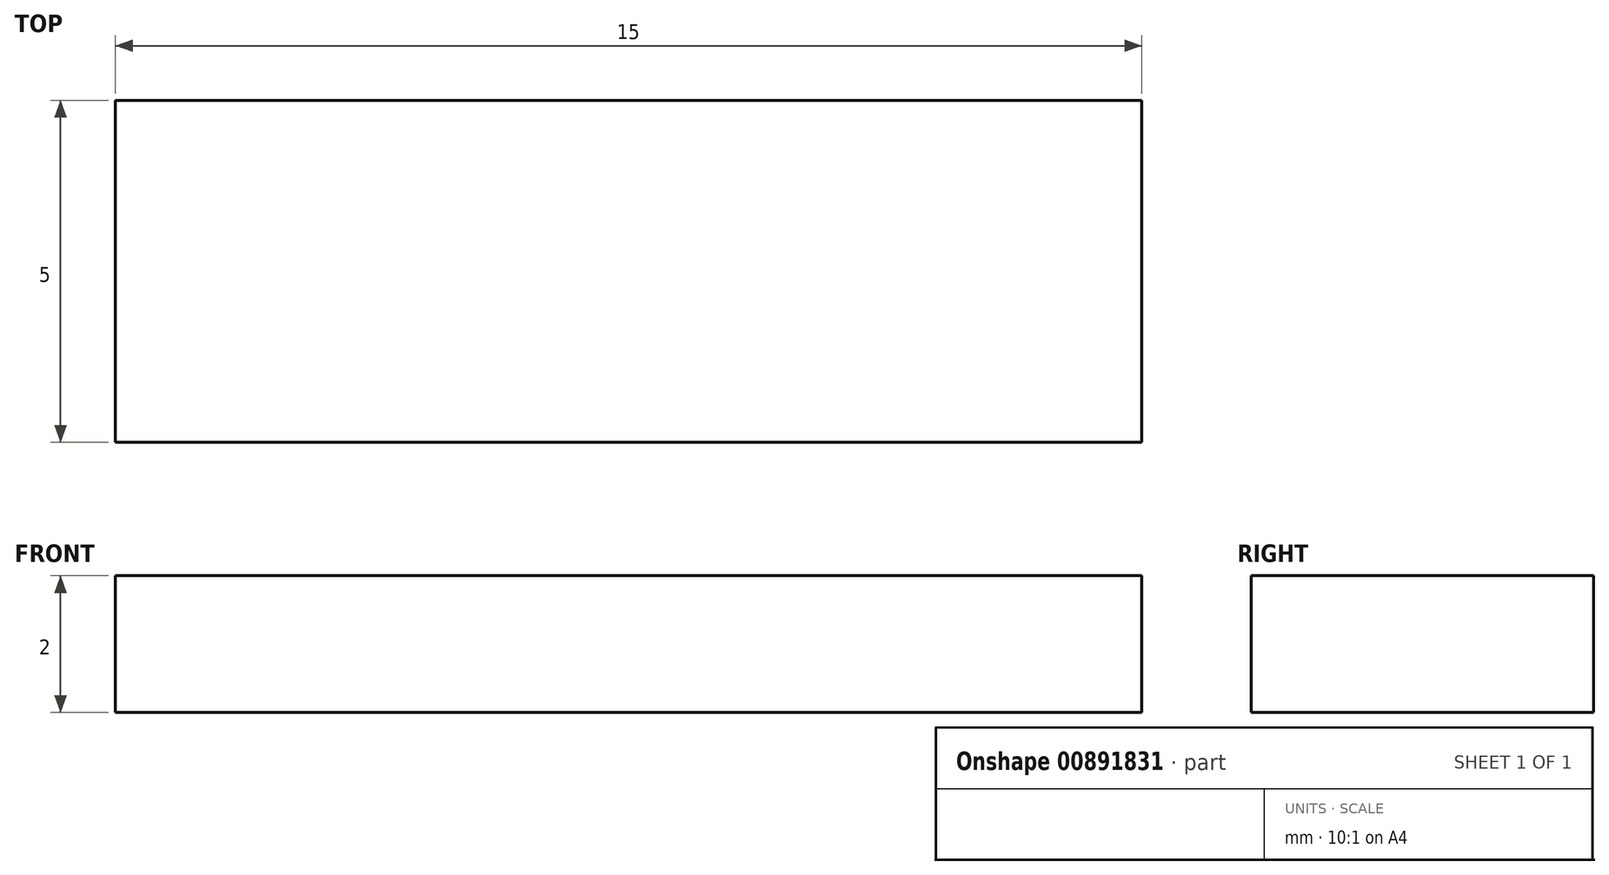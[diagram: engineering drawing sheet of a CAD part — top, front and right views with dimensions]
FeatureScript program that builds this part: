
annotation { "Feature Type Name" : "Feature", "Feature Type Description" : "" }
export const myFeature = defineFeature(function(context is Context, id is Id, definition is map)
    precondition{}
    {
        {
            var Q0;
            Q0=qCreatedBy(makeId("Top.planeOp"),FACE);
            var sketch = newSketch(context, id + "F0", { "sketchPlane" : qUnion([Q0])});
            skLineSegment(sketch, "E0.bottom", {"start": v(42.5, -32.5) * mm, "end": v(-42.5, -32.5) * mm});
            skLineSegment(sketch, "E0.top", {"start": v(42.5, 32.5) * mm, "end": v(-42.5, 32.5) * mm});
            skLineSegment(sketch, "E0.left", {"start": v(42.5, -32.5) * mm, "end": v(42.5, 32.5) * mm});
            skLineSegment(sketch, "E0.right", {"start": v(-42.5, -32.5) * mm, "end": v(-42.5, 32.5) * mm});
            skPoint(sketch, "E0.middle", {"position": v(0, 0) * mm});
            skLineSegment(sketch, "E1.bottom", {"start": v(-27.5, -27.5) * mm, "end": v(-42.5, -27.5) * mm});
            skLineSegment(sketch, "E1.top", {"start": v(-27.5, -32.5) * mm, "end": v(-42.5, -32.5) * mm});
            skLineSegment(sketch, "E1.left", {"start": v(-27.5, -27.5) * mm, "end": v(-27.5, -32.5) * mm});
            skLineSegment(sketch, "E1.right", {"start": v(-42.5, -27.5) * mm, "end": v(-42.5, -32.5) * mm});
            skPoint(sketch, "E1.middle", {"position": v(-35, -30) * mm});
            skSolve(sketch);
        }
        {
            var Q0;
            Q0=makeQuery(id+"F0.imprint","IMPRINT",FACE,{"disambiguationData":[TD([[makeQuery(id+"F0.imprint","IMPRINT",EDGE,{"derivedFrom":sQuery(id+"F0.wireOp",EDGE,"E0.bottom")}),-1.0]])]});
            extrude(context, id + "F1", {"entities" : qUnion([Q0]), "depth" : 2 * mm, "offsetDistance" : 25 * mm});
        }
    });
